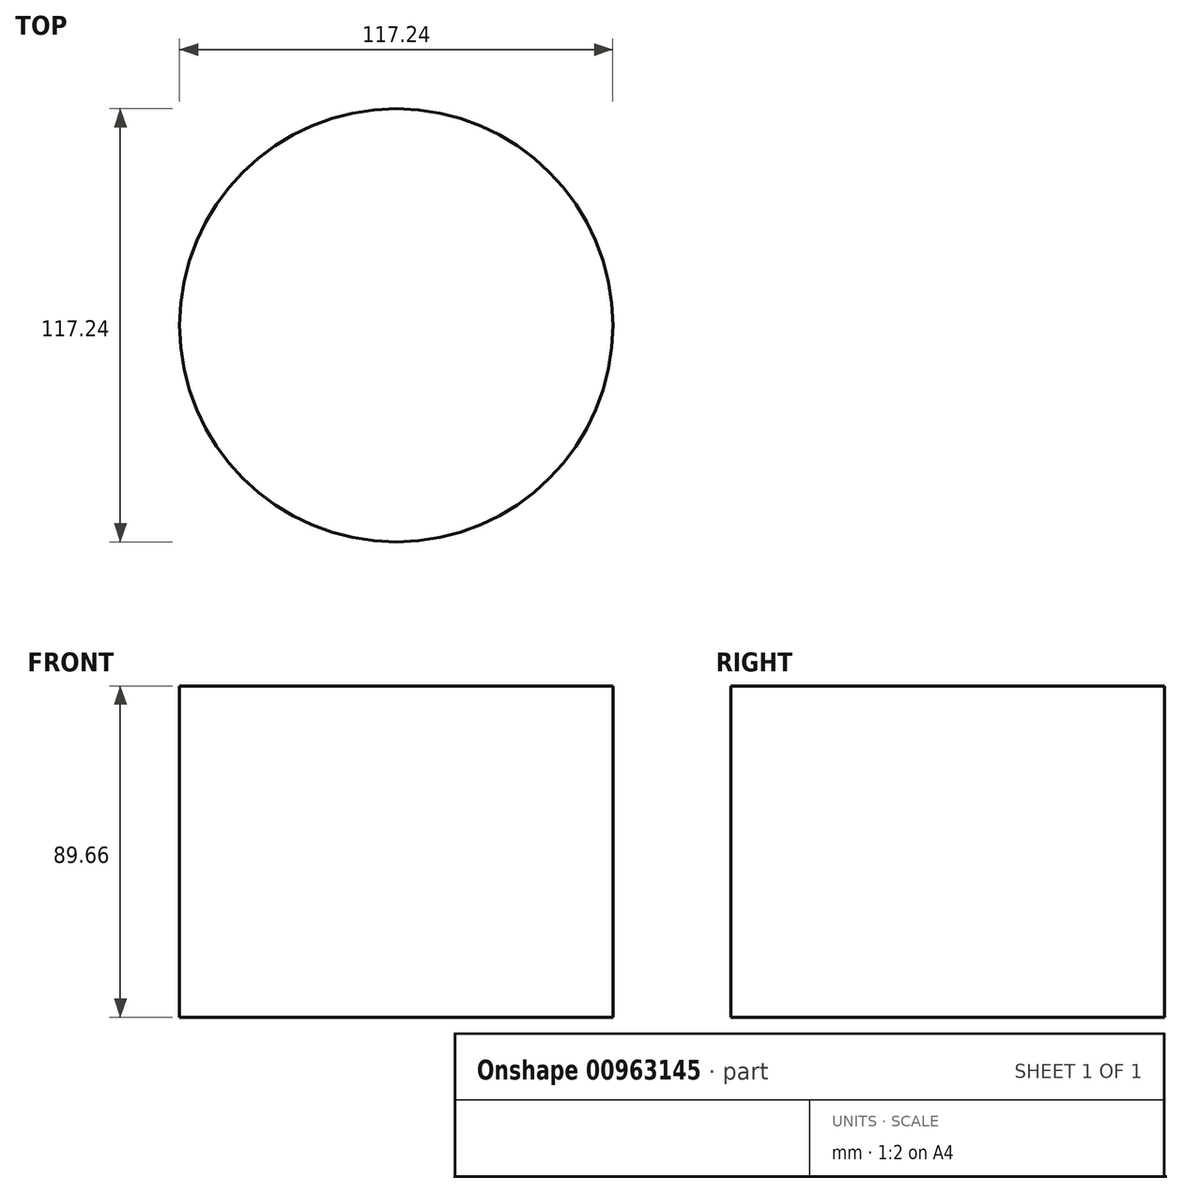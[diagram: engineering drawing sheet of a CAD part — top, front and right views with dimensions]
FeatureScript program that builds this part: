
annotation { "Feature Type Name" : "Feature", "Feature Type Description" : "" }
export const myFeature = defineFeature(function(context is Context, id is Id, definition is map)
    precondition{}
    {
        {
            var Q0;
            Q0=qCreatedBy(makeId("Top.planeOp"),FACE);
            var sketch = newSketch(context, id + "F0", { "sketchPlane" : qUnion([Q0])});
            skCircle(sketch, "E0", {"center": v(0, 0) * mm, "radius": 58.62 * mm});
            skSolve(sketch);
        }
        {
            var Q0;
            Q0=makeQuery(id+"F0.imprint","IMPRINT",FACE,{"disambiguationData":[TD([[makeQuery(id+"F0.imprint","IMPRINT",EDGE,{"derivedFrom":sQuery(id+"F0.wireOp",EDGE,"E0")}),1.0]])]});
            extrude(context, id + "F1", {"entities" : qUnion([Q0]), "depth" : 89.66 * mm, "offsetDistance" : 25.4 * mm});
        }
    });
